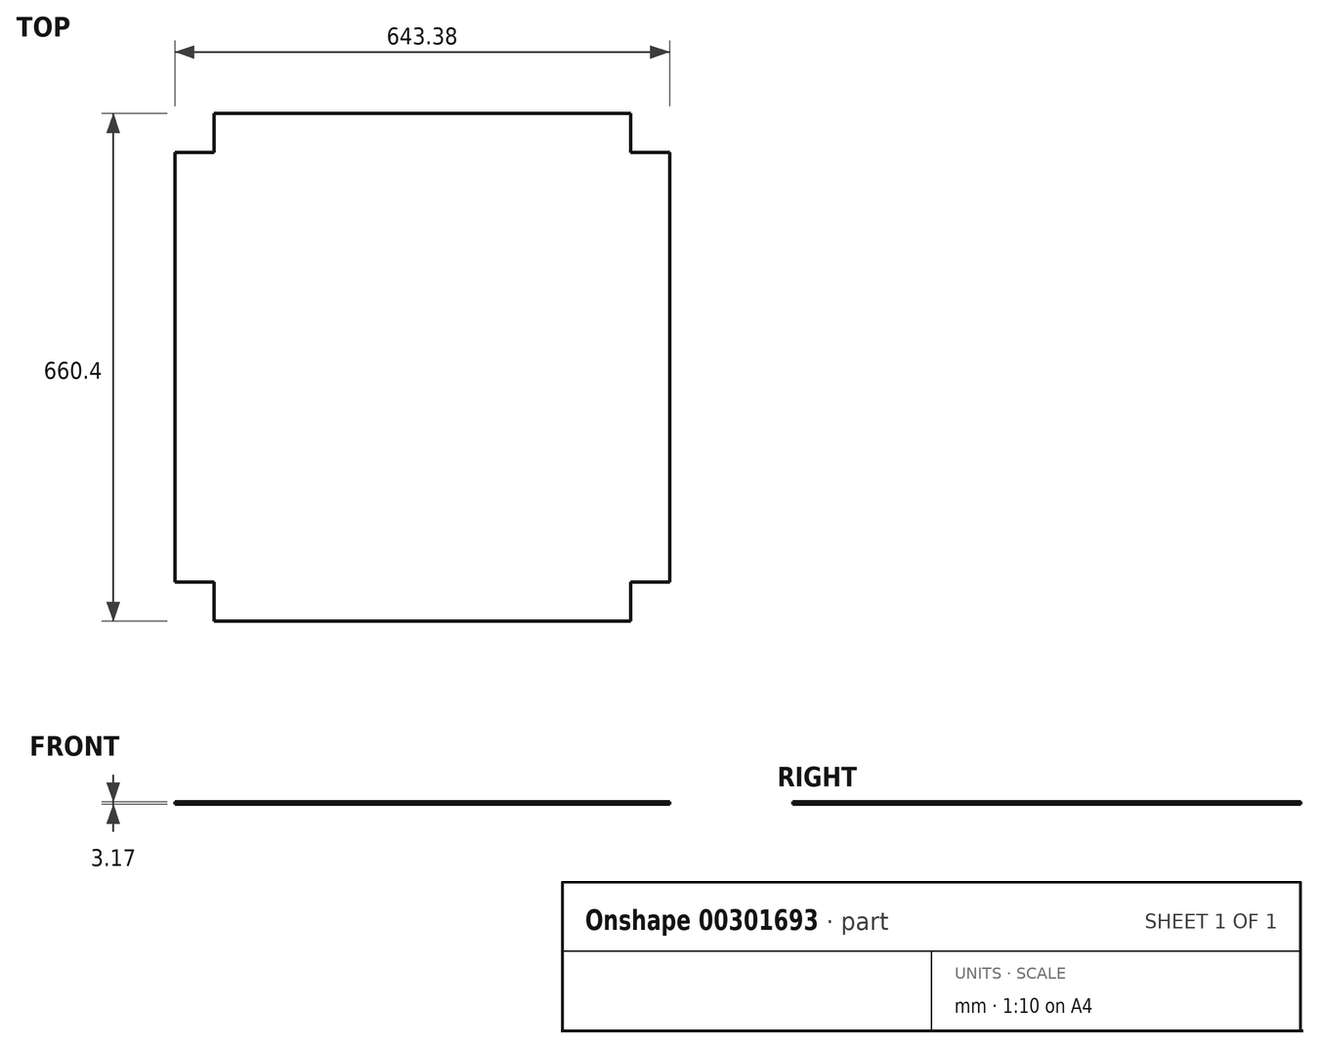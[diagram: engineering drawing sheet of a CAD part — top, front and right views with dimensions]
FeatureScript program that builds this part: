
annotation { "Feature Type Name" : "Feature", "Feature Type Description" : "" }
export const myFeature = defineFeature(function(context is Context, id is Id, definition is map)
    precondition{}
    {
        {
            var Q0;
            Q0=qCreatedBy(makeId("Top.planeOp"),FACE);
            var sketch = newSketch(context, id + "F0", { "sketchPlane" : qUnion([Q0])});
            skLineSegment(sketch, "E0.bottom", {"start": v(-345.43, -330.2) * mm, "end": v(196.35, -330.2) * mm});
            skLineSegment(sketch, "E0.top", {"start": v(-345.43, 330.2) * mm, "end": v(196.35, 330.2) * mm});
            skLineSegment(sketch, "E0.left", {"start": v(-345.43, -330.2) * mm, "end": v(-345.43, 330.2) * mm});
            skLineSegment(sketch, "E0.right", {"start": v(196.35, -330.2) * mm, "end": v(196.35, 330.2) * mm});
            skPoint(sketch, "E0.middle", {"position": v(-74.54, 0) * mm});
            skLineSegment(sketch, "E1.bottom", {"start": v(196.35, -279.4) * mm, "end": v(247.15, -279.4) * mm});
            skLineSegment(sketch, "E1.top", {"start": v(196.35, 279.4) * mm, "end": v(247.15, 279.4) * mm});
            skLineSegment(sketch, "E1.left", {"start": v(196.35, -279.4) * mm, "end": v(196.35, 279.4) * mm});
            skLineSegment(sketch, "E1.right", {"start": v(247.15, -279.4) * mm, "end": v(247.15, 279.4) * mm});
            skPoint(sketch, "E1.middle", {"position": v(221.75, 0) * mm});
            skPoint(sketch, "E1.middle.positionSnap0", {"position": v(196.35, 0) * mm});
            skPoint(sketch, "E1.centerSnap0", {"position": v(196.35, 0) * mm});
            skLineSegment(sketch, "E2.bottom", {"start": v(-345.43, -279.4) * mm, "end": v(-396.23, -279.4) * mm});
            skLineSegment(sketch, "E2.top", {"start": v(-345.43, 279.4) * mm, "end": v(-396.23, 279.4) * mm});
            skLineSegment(sketch, "E2.left", {"start": v(-345.43, -279.4) * mm, "end": v(-345.43, 279.4) * mm});
            skLineSegment(sketch, "E2.right", {"start": v(-396.23, -279.4) * mm, "end": v(-396.23, 279.4) * mm});
            skPoint(sketch, "E2.middle", {"position": v(-370.83, 0) * mm});
            skPoint(sketch, "E2.middle.positionSnap0", {"position": v(-345.43, 0) * mm});
            skPoint(sketch, "E2.centerSnap0", {"position": v(-345.43, 0) * mm});
            skSolve(sketch);
        }
        {
            var Q0;
            Q0 = qSketchRegion(id + "F0", true);
            extrude(context, id + "F1", {"entities" : qUnion([Q0]), "depth" : 3.17 * mm});
        }
    });
